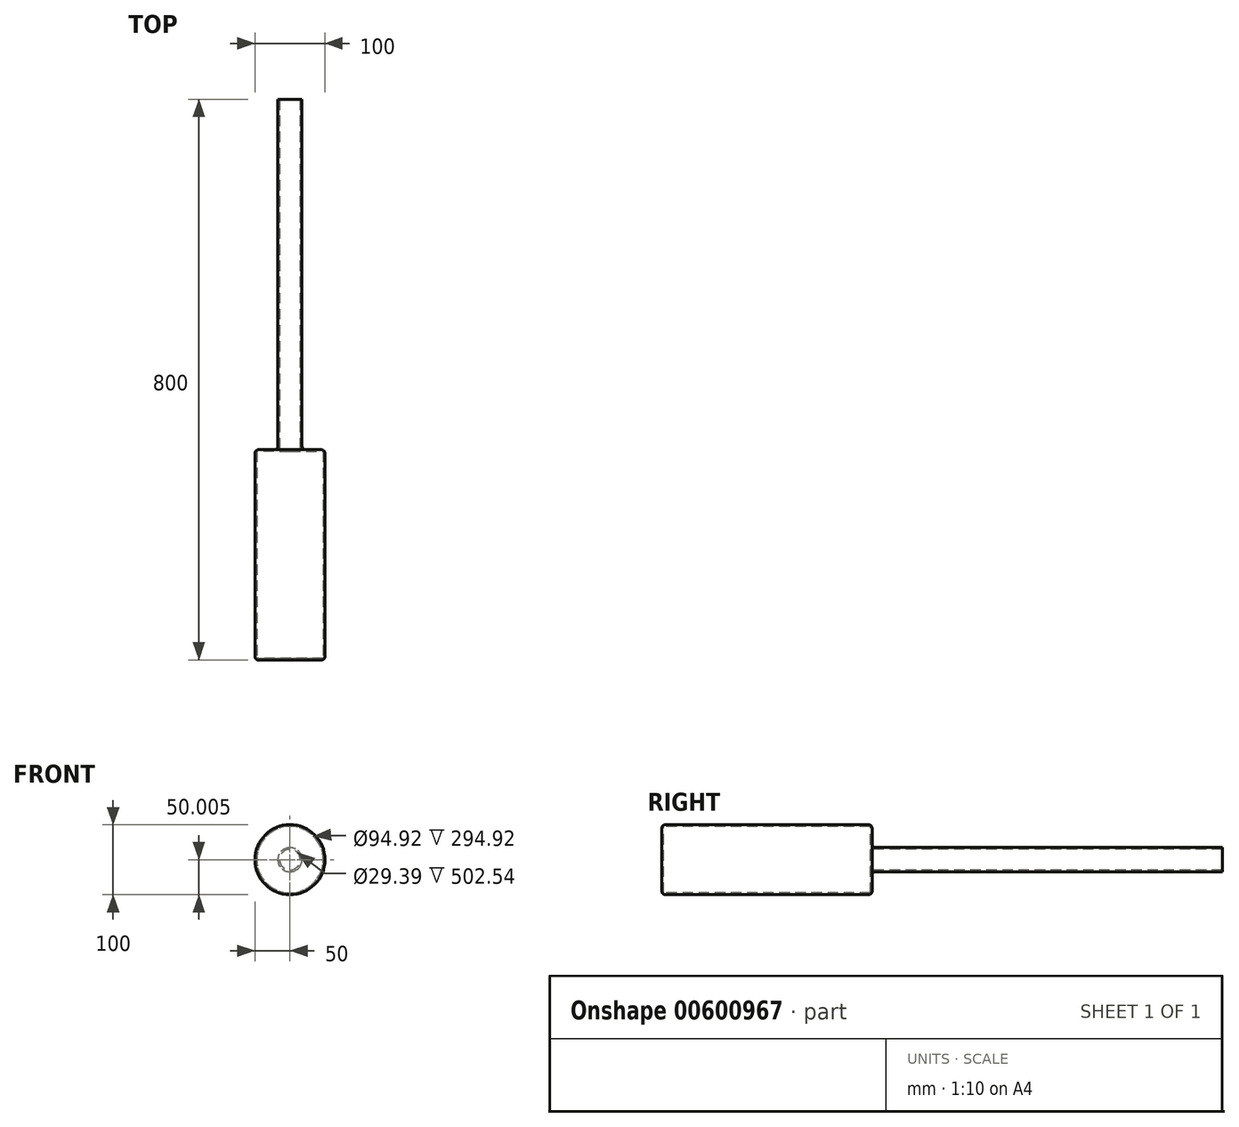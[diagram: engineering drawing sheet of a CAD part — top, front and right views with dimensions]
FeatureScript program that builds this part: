
annotation { "Feature Type Name" : "Feature", "Feature Type Description" : "" }
export const myFeature = defineFeature(function(context is Context, id is Id, definition is map)
    precondition{}
    {
        {
            var Q0;
            Q0=qCreatedBy(makeId("Right.planeOp"),FACE);
            var sketch = newSketch(context, id + "F0", { "sketchPlane" : qUnion([Q0])});
            skLineSegment(sketch, "E0", {"start": v(-221.62, 68.32) * mm, "end": v(78.38, 68.32) * mm});
            skLineSegment(sketch, "E1", {"start": v(78.38, 68.32) * mm, "end": v(78.38, 35.56) * mm});
            skLineSegment(sketch, "E2", {"start": v(78.38, 35.56) * mm, "end": v(578.38, 35.56) * mm});
            skLineSegment(sketch, "E3", {"start": v(578.38, 35.56) * mm, "end": v(578.38, 18.32) * mm});
            skLineSegment(sketch, "E4", {"start": v(-221.62, 18.32) * mm, "end": v(-221.62, 68.32) * mm});
            skLineSegment(sketch, "E5", {"start": v(-221.62, 18.32) * mm, "end": v(578.38, 18.32) * mm});
            skSolve(sketch);
        }
        {
            var Q0;
            Q0=makeQuery(id+"F0.imprint","IMPRINT",FACE,{"disambiguationData":[TD([[makeQuery(id+"F0.imprint","IMPRINT",EDGE,{"derivedFrom":sQuery(id+"F0.wireOp",EDGE,"E0")}),-1.0]])]});
            var Q1;
            Q1=sQuery(id+"F0.wireOp",EDGE,"E5");
            revolve(context, id + "F1", {"entities" : qUnion([Q0]), "axis" : qUnion([Q1]), "revolveType" : RevolveType.FULL});
        }
        {
            var Q0;
            Q0=makeQuery(id+"F1.opRevolve","SWEPT_FACE",FACE,{"disambiguationData":[OSD([sQuery(id+"F0.wireOp",EDGE,"E3")])]});
            shell(context, id + "F2", {"entities" : qUnion([Q0]), "thickness" : 2.54 * mm});
        }
        {
            var Q0;
            Q0=makeQuery(id+"F1.opRevolve","SWEPT_EDGE",EDGE,{"disambiguationData":[OSD([sQuery(id+"F0.wireOp",EDGE,"E0"),sQuery(id+"F0.wireOp",EDGE,"E1")])]});
            var Q1;
            Q1=makeQuery(id+"F1.opRevolve","SWEPT_EDGE",EDGE,{"disambiguationData":[OSD([sQuery(id+"F0.wireOp",EDGE,"E1"),sQuery(id+"F0.wireOp",EDGE,"E2")])]});
            var Q2;
            Q2=makeQuery(id+"F1.opRevolve","SWEPT_EDGE",EDGE,{"disambiguationData":[OSD([sQuery(id+"F0.wireOp",EDGE,"E0"),sQuery(id+"F0.wireOp",EDGE,"E4")])]});
            fillet(context, id + "F3", {"entities" : qUnion([Q0, Q1, Q2]), "radius" : 5.08 * mm, "tangentPropagation" : true, "allowEdgeOverflow" : false});
        }
    });
